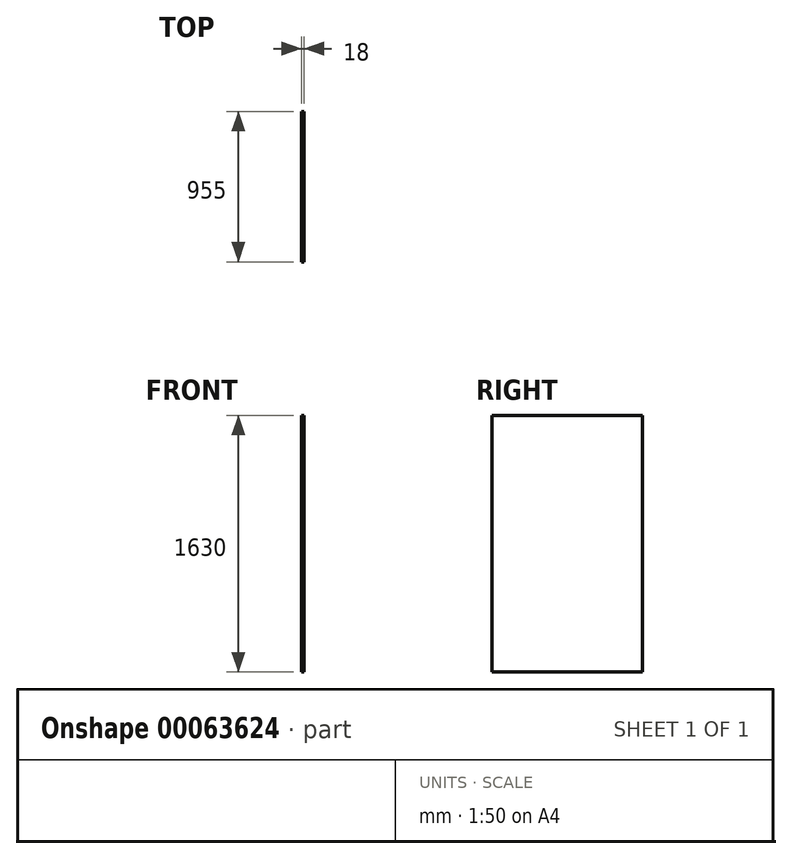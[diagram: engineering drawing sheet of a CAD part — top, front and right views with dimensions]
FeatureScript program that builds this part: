
annotation { "Feature Type Name" : "Feature", "Feature Type Description" : "" }
export const myFeature = defineFeature(function(context is Context, id is Id, definition is map)
    precondition{}
    {
        {
            var Q0;
            Q0=qCreatedBy(makeId("Right.planeOp"),FACE);
            var sketch = newSketch(context, id + "F0", { "sketchPlane" : qUnion([Q0])});
            skLineSegment(sketch, "E0.bottom", {"start": v(0, 0) * mm, "end": v(955, 0) * mm});
            skLineSegment(sketch, "E0.top", {"start": v(0, -1630) * mm, "end": v(955, -1630) * mm});
            skLineSegment(sketch, "E0.left", {"start": v(0, 0) * mm, "end": v(0, -1630) * mm});
            skLineSegment(sketch, "E0.right", {"start": v(955, 0) * mm, "end": v(955, -1630) * mm});
            skSolve(sketch);
        }
        {
            var Q0;
            Q0=makeQuery(id+"F0.imprint","IMPRINT",FACE,{"disambiguationData":[TD([[makeQuery(id+"F0.imprint","IMPRINT",EDGE,{"derivedFrom":sQuery(id+"F0.wireOp",EDGE,"E0.bottom")}),-1.0]])]});
            extrude(context, id + "F1", {"entities" : qUnion([Q0]), "depth" : 18 * mm});
        }
    });
